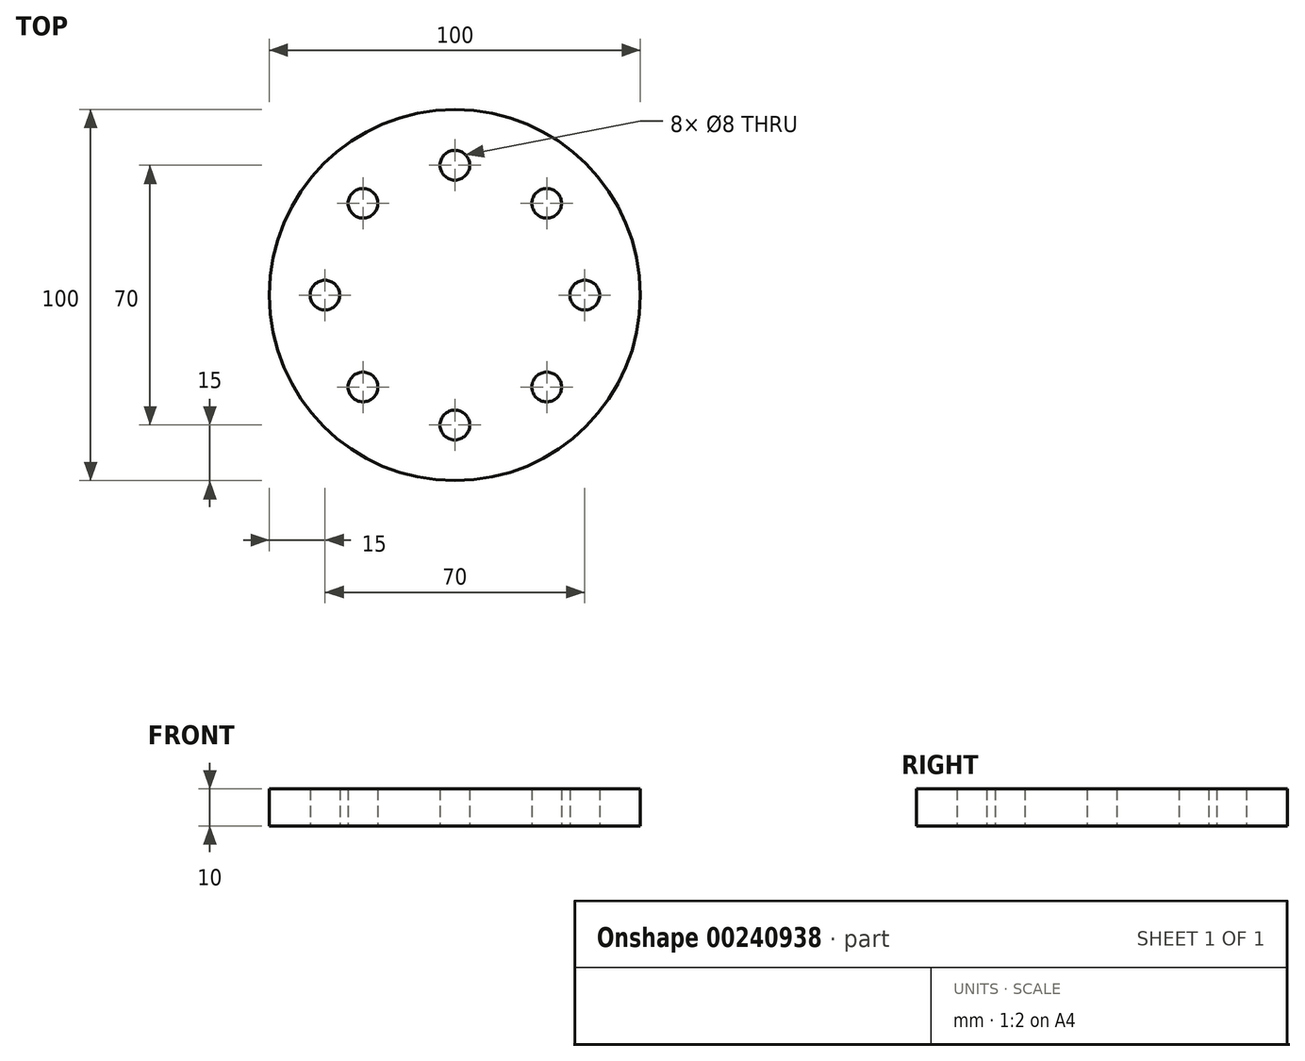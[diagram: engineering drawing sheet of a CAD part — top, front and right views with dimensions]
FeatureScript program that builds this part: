
annotation { "Feature Type Name" : "Feature", "Feature Type Description" : "" }
export const myFeature = defineFeature(function(context is Context, id is Id, definition is map)
    precondition{}
    {
        {
            var Q0;
            Q0=qCreatedBy(makeId("Top.planeOp"),FACE);
            var sketch = newSketch(context, id + "F0", { "sketchPlane" : qUnion([Q0])});
            skCircle(sketch, "E0", {"center": v(0, 0) * mm, "radius": 50 * mm});
            skCircle(sketch, "E1", {"center": v(-35, 0) * mm, "radius": 4 * mm});
            skCircle(sketch, "E2.1.0", {"center": v(-24.75, 24.75) * mm, "radius": 4 * mm});
            skCircle(sketch, "E2.2.0", {"center": v(0, 35) * mm, "radius": 4 * mm});
            skCircle(sketch, "E2.3.0", {"center": v(24.75, 24.75) * mm, "radius": 4 * mm});
            skCircle(sketch, "E2.4.0", {"center": v(35, 0) * mm, "radius": 4 * mm});
            skCircle(sketch, "E2.5.0", {"center": v(24.75, -24.75) * mm, "radius": 4 * mm});
            skCircle(sketch, "E2.6.0", {"center": v(0, -35) * mm, "radius": 4 * mm});
            skCircle(sketch, "E2.7.0", {"center": v(-24.75, -24.75) * mm, "radius": 4 * mm});
            skLineSegment(sketch, "E2.anchor1", {"start": v(0, 0) * mm, "end": v(-35, 0) * mm, "construction": true});
            skLineSegment(sketch, "E2.anchor2", {"start": v(0, 0) * mm, "end": v(-24.75, -24.75) * mm, "construction": true});
            skSolve(sketch);
        }
        {
            var Q0;
            Q0=makeQuery(id+"F0.imprint","IMPRINT",FACE,{"disambiguationData":[TD([[makeQuery(id+"F0.imprint","IMPRINT",EDGE,{"derivedFrom":sQuery(id+"F0.wireOp",EDGE,"E0")}),1.0]])]});
            extrude(context, id + "F1", {"entities" : qUnion([Q0]), "depth" : 10 * mm});
        }
    });
